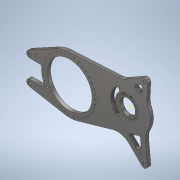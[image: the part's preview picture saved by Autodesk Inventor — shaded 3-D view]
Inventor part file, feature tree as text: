
AUTODESK INVENTOR PART (.ipt)
format: ipt  version: 2021 (Build 250183000, 183)  size: 524,800 bytes
history: native  units: in
note: dims shown in document units (in); Inventor stores cm internally (conversion verified against a paired STEP export)
features: sketch x13, extrude x10, hole x3, projected_geometry x3, chamfer x1, fillet x1
ambient origin geometry x8: Origin, YZ Plane, XZ Plane, XY Plane, X Axis, Y Axis, Z Axis, Center Point
bodies: Body1 (feature_tree)
feature tree (31):
  extrude  "Extrusion24"  Depth=2.16in
  extrude  "Extrusion28"  Depth=9.0in
  hole  "Hole9"  [1 undecoded]
  hole  "Hole11"  [1 undecoded]
  hole  "Hole13"  [1 undecoded]
  extrude  "Extrusion30"  Depth=1.5in
  extrude  "Extrusion31"  Depth=0.5in
  extrude  "Extrusion32"  Depth=0.25in
  extrude  "Extrusion33"  Depth=7.75in
  extrude  "Extrusion34"  Depth=0.25in
  chamfer  "Chamfer2"  Distance=1.0in
  sketch  "Sketch58"  dims[d289=17.223in d290=7.75in]
  extrude  "Extrusion42"  Depth=0.25in
  extrude  "Extrusion46"  Depth=0.25in
  fillet  "Fillet6"  Radius=0.3972in
  sketch  "Sketch71"  dims[d295=0.257in d296=0.75in d297=0.438in d298=0.25in d299=0.5635in d300=1.0in d301=0.8108in d302=0.1718in]
  extrude  "Extrusion50"  Depth=0.25in
  sketch  "Sketch2"  dims[d9=8.5in d92=2.16in]
  sketch  "Sketch35"  dims[d118=0.75in d119=0.75in d120=0.75in d121=0.75in d137=9.0in d142=6.5in]
  projected_geometry  "Projected Loop2"
  sketch  "Sketch36"  dims[d143=1.0in d210=1.0in]
  sketch  "Sketch40"  dims[d211=6.0in d212=6.0in]
  sketch  "Sketch43"  dims[d213=3.718in d214=1.0in]
  sketch  "Sketch47"  dims[d235=10.718in d237=1.5in]
  sketch  "Sketch48"  dims[d239=0.5in d240=0.0in d266=6.75in]
  sketch  "Sketch49"  dims[d267=0.5in d268=0.0in]
  sketch  "Sketch50"  dims[d269=0.386in d270=0.75in d271=0.762in d272=0.25in d273=0.5635in d274=0.484in d275=0.8108in d288=5.0in]
  sketch  "Sketch67"  dims[d291=3.5433in d293=360.0deg]
  sketch  "Sketch72"  dims[d303=15.0deg d316=1.0in d317=0.0481in d318=1.0in d319=0.3972in d322=0.271in d323=0.1355in d324=0.5in d325=0.266in d326=0.75in d327=0.507in d328=0.25in d329=0.5635in d330=1.0in d331=0.8108in d347=1.0in d348=0.0in d349=0.75in d350=0.75in d351=0.5in d353=0.75in d354=0.75in d355=0.25in d356=1.0in d357=0.0in d358=0.25in d359=1.0in d360=0.0in d361=1.0in d362=1.0in d363=0.25in d364=1.0in d365=0.0in d366=2.5in d367=1.0in d368=0.0in d373=0.0156in d374=0.125in d375=45.0deg d435=1.0in d436=0.0in d456=2.35in d457=8.715in d466=3.7in d467=5.0in d468=45.0deg d469=1.5in d470=1.0in d471=0.0in d472=0.25in d502=0.315in d503=1.0in d504=0.0in]
  projected_geometry  "Project Cut Edges2"
  projected_geometry  "Project Cut Edges4"
note: 3 required parameter values undecoded (feature->parameter linkage not recoverable at this tier; creation-order binding heuristic only, values carry confidence <= 0.55)
